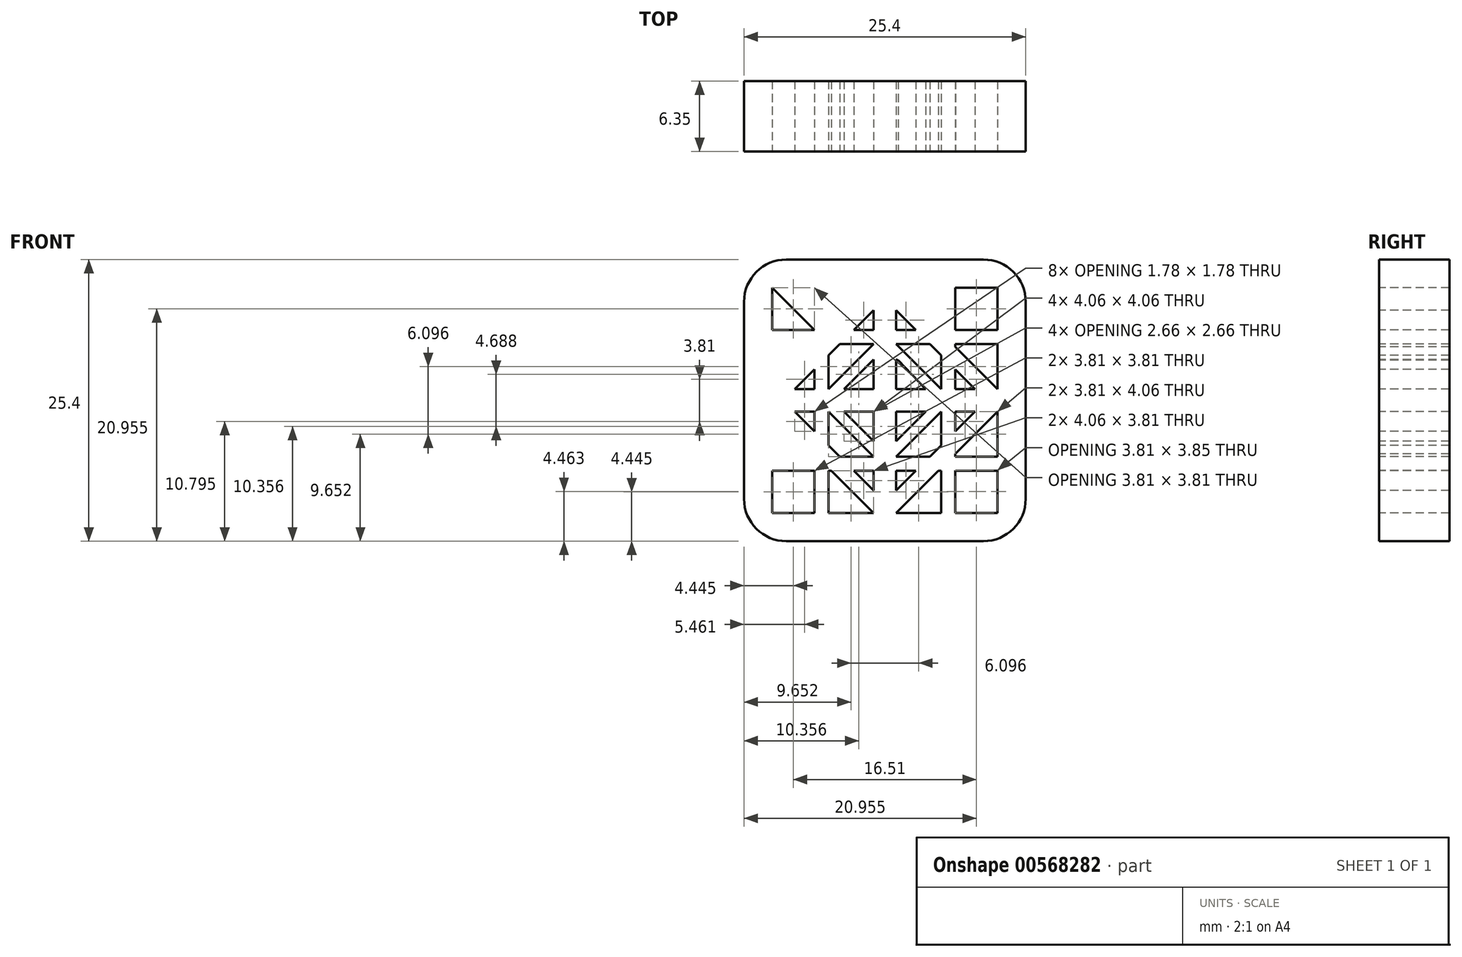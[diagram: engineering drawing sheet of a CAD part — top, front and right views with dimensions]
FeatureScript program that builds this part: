
annotation { "Feature Type Name" : "Feature", "Feature Type Description" : "" }
export const myFeature = defineFeature(function(context is Context, id is Id, definition is map)
    precondition{}
    {
        {
            var Q0;
            Q0=qCreatedBy(makeId("Front.planeOp"),FACE);
            var sketch = newSketch(context, id + "F0", { "sketchPlane" : qUnion([Q0])});
            skLineSegment(sketch, "E0", {"start": v(0, 0) * mm, "end": v(0, 25.4) * mm});
            skLineSegment(sketch, "E1", {"start": v(0, 25.4) * mm, "end": v(25.4, 25.4) * mm});
            skLineSegment(sketch, "E2", {"start": v(25.4, 25.4) * mm, "end": v(25.4, 0) * mm});
            skLineSegment(sketch, "E3", {"start": v(25.4, 0) * mm, "end": v(0, 0) * mm});
            skSolve(sketch);
        }
        {
            var Q0;
            Q0 = qSketchRegion(id + "F0", true);
            extrude(context, id + "F1", {"entities" : qUnion([Q0]), "depth" : 6.35 * mm, "offsetDistance" : 25.4 * mm});
        }
        {
            var Q0;
            Q0=qCreatedBy(makeId("Front.planeOp"),FACE);
            cPlane(context, id + "F2", {"entities" : qUnion([Q0]), "cplaneType" : CPlaneType.OFFSET, "offset" : 6.35 * mm, "width" : 152.4 * mm, "height" : 152.4 * mm});
        }
        {
            var Q0;
            Q0=qCreatedBy(id+"F2.planeOp",FACE);
            var sketch = newSketch(context, id + "F3", { "sketchPlane" : qUnion([Q0])});
            skLineSegment(sketch, "E4", {"start": v(0, 3.8) * mm, "end": v(0, 21.59) * mm});
            skLineSegment(sketch, "E5", {"start": v(3.8, 25.4) * mm, "end": v(21.59, 25.4) * mm});
            skLineSegment(sketch, "E6", {"start": v(25.4, 21.59) * mm, "end": v(25.4, 3.8) * mm});
            skLineSegment(sketch, "E7", {"start": v(21.59, 0) * mm, "end": v(3.8, 0) * mm});
            skPoint(sketch, "E8.0.internal.orphan", {"position": v(0, 12.7) * mm});
            skPoint(sketch, "E8.1.internal.orphan", {"position": v(12.7, 25.4) * mm});
            skPoint(sketch, "E8.2.internal.orphan", {"position": v(25.4, 12.7) * mm});
            skPoint(sketch, "E8.3.internal.orphan", {"position": v(12.7, 0) * mm});
            skPoint(sketch, "E9.center.orphan", {"position": v(12.7, 12.7) * mm});
            skArc(sketch, "E10", {"start": v(13.9, 16.32) * mm, "mid": v(13.8, 16.35) * mm, "end": v(13.72, 16.37) * mm});
            skLineSegment(sketch, "E11", {"start": v(12.7, 19.69) * mm, "end": v(12.7, 19.05) * mm});
            skPoint(sketch, "E11.endSnap0", {"position": v(12.7, 19.69) * mm});
            skLineSegment(sketch, "E12", {"start": v(2.54, 12.7) * mm, "end": v(8.9, 12.7) * mm});
            skLineSegment(sketch, "E13", {"start": v(16.51, 12.7) * mm, "end": v(22.86, 12.7) * mm});
            skLineSegment(sketch, "E14", {"start": v(12.7, 22.86) * mm, "end": v(22.86, 12.7) * mm});
            skLineSegment(sketch, "E15", {"start": v(22.35, 12.2) * mm, "end": v(22.86, 12.7) * mm});
            skLineSegment(sketch, "E16", {"start": v(12.7, 22.86) * mm, "end": v(12.2, 22.35) * mm});
            skLineSegment(sketch, "E17", {"start": v(17.78, 17.78) * mm, "end": v(8.13, 8.13) * mm});
            skLineSegment(sketch, "E18", {"start": v(8.13, 17.27) * mm, "end": v(17.78, 7.62) * mm});
            skLineSegment(sketch, "E19", {"start": v(2.54, 12.7) * mm, "end": v(0, 12.7) * mm});
            skLineSegment(sketch, "E20", {"start": v(12.7, 22.86) * mm, "end": v(0, 22.86) * mm});
            skLineSegment(sketch, "E21", {"start": v(12.7, 22.86) * mm, "end": v(25.4, 22.86) * mm});
            skLineSegment(sketch, "E22", {"start": v(22.86, 12.7) * mm, "end": v(22.86, 25.4) * mm});
            skLineSegment(sketch, "E23", {"start": v(22.86, 12.7) * mm, "end": v(22.86, 0) * mm});
            skLineSegment(sketch, "E24", {"start": v(12.7, 2.54) * mm, "end": v(25.4, 2.54) * mm});
            skLineSegment(sketch, "E25", {"start": v(12.7, 2.54) * mm, "end": v(0, 2.54) * mm});
            skLineSegment(sketch, "E26", {"start": v(2.54, 12.7) * mm, "end": v(2.54, 0) * mm});
            skLineSegment(sketch, "E27", {"start": v(2.54, 12.7) * mm, "end": v(2.54, 25.4) * mm});
            skLineSegment(sketch, "E28", {"start": v(2.54, 22.86) * mm, "end": v(7.11, 18.29) * mm});
            skLineSegment(sketch, "E29", {"start": v(17.78, 17.78) * mm, "end": v(22.86, 22.86) * mm});
            skLineSegment(sketch, "E30", {"start": v(18.03, 7.42) * mm, "end": v(22.86, 2.54) * mm});
            skLineSegment(sketch, "E31", {"start": v(2.54, 2.54) * mm, "end": v(7.11, 7.11) * mm});
            skLineSegment(sketch, "E32", {"start": v(22.86, 12.7) * mm, "end": v(25.4, 12.7) * mm});
            skLineSegment(sketch, "E33", {"start": v(2.54, 22.86) * mm, "end": v(12.7, 22.86) * mm});
            skLineSegment(sketch, "E34", {"start": v(12.7, 22.86) * mm, "end": v(22.86, 22.86) * mm});
            skLineSegment(sketch, "E35", {"start": v(22.86, 22.86) * mm, "end": v(22.86, 12.7) * mm});
            skLineSegment(sketch, "E36", {"start": v(22.86, 12.7) * mm, "end": v(22.86, 2.54) * mm});
            skLineSegment(sketch, "E37", {"start": v(6.35, 22.86) * mm, "end": v(6.35, 17.53) * mm});
            skLineSegment(sketch, "E38", {"start": v(6.35, 2.54) * mm, "end": v(7.62, 2.54) * mm});
            skLineSegment(sketch, "E39", {"start": v(7.62, 2.54) * mm, "end": v(7.62, 6.6) * mm});
            skLineSegment(sketch, "E40", {"start": v(7.62, 22.86) * mm, "end": v(6.35, 22.86) * mm});
            skLineSegment(sketch, "E41", {"start": v(19.05, 22.86) * mm, "end": v(19.05, 2.54) * mm});
            skLineSegment(sketch, "E42", {"start": v(19.05, 2.54) * mm, "end": v(17.78, 2.54) * mm});
            skLineSegment(sketch, "E43", {"start": v(17.78, 2.54) * mm, "end": v(17.78, 22.86) * mm});
            skLineSegment(sketch, "E44", {"start": v(17.78, 22.86) * mm, "end": v(19.05, 22.86) * mm});
            skLineSegment(sketch, "E45", {"start": v(2.54, 19.05) * mm, "end": v(7.87, 19.05) * mm});
            skLineSegment(sketch, "E46", {"start": v(22.86, 19.05) * mm, "end": v(22.86, 17.78) * mm});
            skLineSegment(sketch, "E47", {"start": v(22.86, 17.78) * mm, "end": v(8.64, 17.78) * mm});
            skLineSegment(sketch, "E48", {"start": v(2.54, 17.78) * mm, "end": v(2.54, 19.05) * mm});
            skLineSegment(sketch, "E49", {"start": v(2.54, 6.35) * mm, "end": v(22.86, 6.35) * mm});
            skLineSegment(sketch, "E50", {"start": v(22.86, 6.35) * mm, "end": v(22.86, 7.62) * mm});
            skLineSegment(sketch, "E51", {"start": v(22.86, 7.62) * mm, "end": v(8.64, 7.62) * mm});
            skLineSegment(sketch, "E52", {"start": v(2.54, 7.62) * mm, "end": v(2.54, 6.35) * mm});
            skLineSegment(sketch, "E53", {"start": v(7.62, 22.86) * mm, "end": v(12.7, 22.86) * mm});
            skLineSegment(sketch, "E54", {"start": v(17.78, 22.86) * mm, "end": v(17.78, 17.78) * mm});
            skLineSegment(sketch, "E55", {"start": v(17.78, 12.7) * mm, "end": v(17.78, 7.62) * mm});
            skLineSegment(sketch, "E56", {"start": v(11.68, 20.83) * mm, "end": v(11.68, 4.57) * mm});
            skLineSegment(sketch, "E57", {"start": v(11.68, 2.54) * mm, "end": v(13.72, 2.54) * mm});
            skLineSegment(sketch, "E58", {"start": v(13.72, 2.54) * mm, "end": v(13.72, 22.86) * mm});
            skLineSegment(sketch, "E59", {"start": v(13.72, 22.86) * mm, "end": v(11.68, 22.86) * mm});
            skLineSegment(sketch, "E60.trimOffspring", {"start": v(12.7, 17.78) * mm, "end": v(12.7, 16.51) * mm});
            skLineSegment(sketch, "E61.trimOffspring", {"start": v(12.7, 19.05) * mm, "end": v(12.7, 19.69) * mm});
            skLineSegment(sketch, "E62", {"start": v(2.54, 17.78) * mm, "end": v(2.54, 12.7) * mm});
            skLineSegment(sketch, "E63", {"start": v(2.54, 7.62) * mm, "end": v(2.54, 12.7) * mm});
            skLineSegment(sketch, "E64", {"start": v(4.57, 11.68) * mm, "end": v(20.83, 11.68) * mm});
            skLineSegment(sketch, "E65", {"start": v(22.86, 11.68) * mm, "end": v(22.86, 13.72) * mm});
            skLineSegment(sketch, "E66", {"start": v(22.86, 13.72) * mm, "end": v(4.57, 13.72) * mm});
            skLineSegment(sketch, "E67", {"start": v(2.54, 13.72) * mm, "end": v(2.54, 11.68) * mm});
            skPoint(sketch, "E68.visualSharp", {"position": v(0, 25.4) * mm});
            skArc(sketch, "E68.filletArc", {"start": v(3.81, 25.4) * mm, "mid": v(1.12, 24.28) * mm, "end": v(0, 21.59) * mm});
            skPoint(sketch, "E69.visualSharp", {"position": v(25.4, 25.4) * mm});
            skArc(sketch, "E69.filletArc", {"start": v(25.4, 21.59) * mm, "mid": v(24.28, 24.28) * mm, "end": v(21.59, 25.4) * mm});
            skPoint(sketch, "E70.visualSharp", {"position": v(25.4, 0) * mm});
            skArc(sketch, "E70.filletArc", {"start": v(21.59, 0) * mm, "mid": v(24.28, 1.12) * mm, "end": v(25.4, 3.8) * mm});
            skPoint(sketch, "E71.visualSharp", {"position": v(0, 0) * mm});
            skArc(sketch, "E71.filletArc", {"start": v(0, 3.8) * mm, "mid": v(1.12, 1.12) * mm, "end": v(3.8, 0) * mm});
            skLineSegment(sketch, "E72", {"start": v(12.7, 21.84) * mm, "end": v(21.84, 12.7) * mm});
            skLineSegment(sketch, "E73", {"start": v(22.86, 13.72) * mm, "end": v(13.72, 22.86) * mm});
            skLineSegment(sketch, "E74", {"start": v(11.68, 22.86) * mm, "end": v(13.72, 22.86) * mm});
            skLineSegment(sketch, "E75", {"start": v(12.7, 3.56) * mm, "end": v(22.86, 13.72) * mm});
            skLineSegment(sketch, "E76", {"start": v(22.86, 11.68) * mm, "end": v(13.72, 2.54) * mm});
            skLineSegment(sketch, "E77", {"start": v(2.54, 11.68) * mm, "end": v(11.68, 2.54) * mm});
            skLineSegment(sketch, "E78", {"start": v(3.56, 12.7) * mm, "end": v(12.7, 3.56) * mm});
            skLineSegment(sketch, "E79", {"start": v(2.54, 11.68) * mm, "end": v(2.54, 13.72) * mm});
            skLineSegment(sketch, "E80", {"start": v(2.54, 13.72) * mm, "end": v(11.68, 22.86) * mm});
            skLineSegment(sketch, "E81", {"start": v(13.72, 22.86) * mm, "end": v(13.2, 22.35) * mm});
            skLineSegment(sketch, "E82.trimOffspring", {"start": v(6.6, 7.62) * mm, "end": v(2.54, 7.62) * mm});
            skLineSegment(sketch, "E83.bottom", {"start": v(0, 0) * mm, "end": v(25.4, 0) * mm});
            skLineSegment(sketch, "E83.top", {"start": v(0, 25.4) * mm, "end": v(25.4, 25.4) * mm});
            skLineSegment(sketch, "E83.left", {"start": v(0, 0) * mm, "end": v(0, 25.4) * mm});
            skLineSegment(sketch, "E83.right", {"start": v(25.4, 0) * mm, "end": v(25.4, 25.4) * mm});
            skLineSegment(sketch, "E84.trimOffspring", {"start": v(22.35, 12.2) * mm, "end": v(22.86, 11.68) * mm});
            skLineSegment(sketch, "E85.trimOffspring", {"start": v(7.62, 8.64) * mm, "end": v(7.62, 16.76) * mm});
            skPoint(sketch, "E86.orphan", {"position": v(7.62, 7.62) * mm});
            skLineSegment(sketch, "E87.trimOffspring", {"start": v(6.35, 15.5) * mm, "end": v(6.35, 2.54) * mm});
            skLineSegment(sketch, "E88.trimOffspring", {"start": v(6.6, 17.78) * mm, "end": v(2.54, 17.78) * mm});
            skLineSegment(sketch, "E89.trimOffspring", {"start": v(7.62, 18.8) * mm, "end": v(7.62, 22.86) * mm});
            skPoint(sketch, "E90.orphan", {"position": v(7.62, 17.78) * mm});
            skLineSegment(sketch, "E91.trimOffspring", {"start": v(9.9, 19.05) * mm, "end": v(22.86, 19.05) * mm});
            skLineSegment(sketch, "E92.trimOffspring", {"start": v(12.7, 21.84) * mm, "end": v(3.56, 12.7) * mm});
            skLineSegment(sketch, "E93.trimOffspring", {"start": v(15.08, 15.08) * mm, "end": v(16.37, 13.72) * mm});
            skPoint(sketch, "E94.start.orphan", {"position": v(13.72, 16.51) * mm});
            skLineSegment(sketch, "E95", {"start": v(13.72, 16.51) * mm, "end": v(16.37, 13.72) * mm});
            skLineSegment(sketch, "E96", {"start": v(13.72, 17.78) * mm, "end": v(17.78, 13.72) * mm});
            skLineSegment(sketch, "E97", {"start": v(17.78, 13.72) * mm, "end": v(16.37, 13.72) * mm});
            skLineSegment(sketch, "E98", {"start": v(13.72, 16.51) * mm, "end": v(13.72, 17.78) * mm});
            skLineSegment(sketch, "E99", {"start": v(13.72, 9.03) * mm, "end": v(16.37, 11.68) * mm});
            skLineSegment(sketch, "E100", {"start": v(13.72, 7.62) * mm, "end": v(13.72, 9.03) * mm});
            skLineSegment(sketch, "E101", {"start": v(17.78, 11.68) * mm, "end": v(13.72, 7.62) * mm});
            skLineSegment(sketch, "E102", {"start": v(16.37, 11.68) * mm, "end": v(17.78, 11.68) * mm});
            skLineSegment(sketch, "E103", {"start": v(7.62, 12.7) * mm, "end": v(8.9, 12.7) * mm});
            skLineSegment(sketch, "E104", {"start": v(11.68, 16.37) * mm, "end": v(11.68, 17.78) * mm});
            skLineSegment(sketch, "E105", {"start": v(7.62, 11.68) * mm, "end": v(11.68, 7.62) * mm});
            skLineSegment(sketch, "E106", {"start": v(11.68, 7.62) * mm, "end": v(11.68, 9.03) * mm});
            skLineSegment(sketch, "E107", {"start": v(9.03, 11.68) * mm, "end": v(11.68, 9.03) * mm});
            skLineSegment(sketch, "E108", {"start": v(9.03, 11.68) * mm, "end": v(7.62, 11.68) * mm});
            skArc(sketch, "E109.trimOffspring", {"start": v(9.03, 13.72) * mm, "mid": v(11.68, 9.03) * mm, "end": v(16.37, 11.68) * mm});
            skLineSegment(sketch, "E110", {"start": v(9.03, 13.72) * mm, "end": v(11.68, 16.37) * mm});
            skLineSegment(sketch, "E111", {"start": v(11.68, 17.78) * mm, "end": v(11.68, 16.37) * mm});
            skLineSegment(sketch, "E112", {"start": v(7.62, 13.72) * mm, "end": v(11.68, 17.78) * mm});
            skLineSegment(sketch, "E113", {"start": v(7.62, 13.72) * mm, "end": v(9.03, 13.72) * mm});
            skSolve(sketch);
        }
        {
            var Q0;
            {var subQ0=sQuery(id+"F3.wireOp",EDGE,"E33");Q0=makeQuery(id+"F3.imprint","IMPRINT",FACE,{"disambiguationData":[TD([[makeQuery(id+"F3.imprint","IMPRINT",EDGE,{"derivedFrom":subQ0}),-1.0]])]});}
            var Q1;
            {var subQ1=sQuery(id+"F3.wireOp",EDGE,"E27");var subQ3=sQuery(id+"F3.wireOp",EDGE,"E45");var subQ4=makeQuery(id+"F3.imprint","INTERSECT",VERTEX,{"derivedFrom":[subQ1,subQ3,sQuery(id+"F3.wireOp",EDGE,"E48")]});Q1=makeQuery(id+"F3.imprint","IMPRINT",FACE,{"disambiguationData":[TD([[makeQuery(id+"F3.imprint","IMPRINT",EDGE,{"disambiguationData":[TD([[subQ4,-1.0]])],"derivedFrom":subQ3}),1.0]])]});}
            var Q2;
            {var subQ5=sQuery(id+"F3.wireOp",EDGE,"E62");Q2=makeQuery(id+"F3.imprint","IMPRINT",FACE,{"disambiguationData":[TD([[makeQuery(id+"F3.imprint","IMPRINT",EDGE,{"derivedFrom":subQ5}),1.0]])]});}
            var Q3;
            {var subQ0=sQuery(id+"F3.wireOp",EDGE,"E92.trimOffspring");var subQ1=sQuery(id+"F3.wireOp",EDGE,"E66");var subQ2=makeQuery(id+"F3.imprint","INTERSECT",VERTEX,{"derivedFrom":[subQ1,subQ0]});Q3=makeQuery(id+"F3.imprint","IMPRINT",FACE,{"disambiguationData":[TD([[makeQuery(id+"F3.imprint","IMPRINT",EDGE,{"disambiguationData":[TD([[subQ2,1.0]])],"derivedFrom":subQ1}),-1.0]])]});}
            var Q4;
            {var subQ0=sQuery(id+"F3.wireOp",EDGE,"E78");var subQ1=sQuery(id+"F3.wireOp",EDGE,"E64");var subQ2=makeQuery(id+"F3.imprint","INTERSECT",VERTEX,{"derivedFrom":[subQ1,subQ0]});Q4=makeQuery(id+"F3.imprint","IMPRINT",FACE,{"disambiguationData":[TD([[makeQuery(id+"F3.imprint","IMPRINT",EDGE,{"disambiguationData":[TD([[subQ2,-1.0]])],"derivedFrom":subQ1}),-1.0]])]});}
            var Q5;
            {var subQ0=sQuery(id+"F3.wireOp",EDGE,"E63");Q5=makeQuery(id+"F3.imprint","IMPRINT",FACE,{"disambiguationData":[TD([[makeQuery(id+"F3.imprint","IMPRINT",EDGE,{"derivedFrom":subQ0}),-1.0]])]});}
            var Q6;
            {var subQ0=sQuery(id+"F3.wireOp",EDGE,"E107");var subQ1=sQuery(id+"F3.wireOp",EDGE,"E17");var subQ2=makeQuery(id+"F3.imprint","INTERSECT",VERTEX,{"derivedFrom":[subQ1,subQ0]});Q6=makeQuery(id+"F3.imprint","IMPRINT",FACE,{"disambiguationData":[TD([[makeQuery(id+"F3.imprint","IMPRINT",EDGE,{"disambiguationData":[TD([[subQ2,1.0]])],"derivedFrom":subQ1}),-1.0]])]});}
            var Q7;
            {var subQ0=sQuery(id+"F3.wireOp",EDGE,"E107");var subQ1=sQuery(id+"F3.wireOp",EDGE,"E17");var subQ2=makeQuery(id+"F3.imprint","INTERSECT",VERTEX,{"derivedFrom":[subQ1,subQ0]});Q7=makeQuery(id+"F3.imprint","IMPRINT",FACE,{"disambiguationData":[TD([[makeQuery(id+"F3.imprint","IMPRINT",EDGE,{"disambiguationData":[TD([[subQ2,1.0]])],"derivedFrom":subQ1}),1.0]])]});}
            var Q8;
            {var subQ0=sQuery(id+"F3.wireOp",EDGE,"E10");Q8=makeQuery(id+"F3.imprint","IMPRINT",FACE,{"disambiguationData":[TD([[makeQuery(id+"F3.imprint","IMPRINT",EDGE,{"derivedFrom":subQ0}),1.0]])]});}
            var Q9;
            {var subQ0=sQuery(id+"F3.wireOp",EDGE,"E95");var subQ1=sQuery(id+"F3.wireOp",EDGE,"E17");var subQ2=makeQuery(id+"F3.imprint","INTERSECT",VERTEX,{"derivedFrom":[subQ1,subQ0]});Q9=makeQuery(id+"F3.imprint","IMPRINT",FACE,{"disambiguationData":[TD([[makeQuery(id+"F3.imprint","IMPRINT",EDGE,{"disambiguationData":[TD([[subQ2,-1.0]])],"derivedFrom":subQ1}),1.0]])]});}
            var Q10;
            {var subQ0=sQuery(id+"F3.wireOp",EDGE,"E99");var subQ1=sQuery(id+"F3.wireOp",EDGE,"E18");var subQ2=makeQuery(id+"F3.imprint","INTERSECT",VERTEX,{"derivedFrom":[subQ1,subQ0]});Q10=makeQuery(id+"F3.imprint","IMPRINT",FACE,{"disambiguationData":[TD([[makeQuery(id+"F3.imprint","IMPRINT",EDGE,{"disambiguationData":[TD([[subQ2,1.0]])],"derivedFrom":subQ1}),1.0]])]});}
            var Q11;
            {var subQ0=sQuery(id+"F3.wireOp",EDGE,"E99");var subQ1=sQuery(id+"F3.wireOp",EDGE,"E18");var subQ2=makeQuery(id+"F3.imprint","INTERSECT",VERTEX,{"derivedFrom":[subQ1,subQ0]});Q11=makeQuery(id+"F3.imprint","IMPRINT",FACE,{"disambiguationData":[TD([[makeQuery(id+"F3.imprint","IMPRINT",EDGE,{"disambiguationData":[TD([[subQ2,1.0]])],"derivedFrom":subQ1}),-1.0]])]});}
            var Q12;
            {var subQ0=sQuery(id+"F3.wireOp",EDGE,"E78");var subQ1=sQuery(id+"F3.wireOp",EDGE,"E17");var subQ2=makeQuery(id+"F3.imprint","INTERSECT",VERTEX,{"derivedFrom":[subQ1,subQ0]});Q12=makeQuery(id+"F3.imprint","IMPRINT",FACE,{"disambiguationData":[TD([[makeQuery(id+"F3.imprint","IMPRINT",EDGE,{"disambiguationData":[TD([[subQ2,1.0]])],"derivedFrom":subQ1}),1.0]])]});}
            var Q13;
            {var subQ0=sQuery(id+"F3.wireOp",EDGE,"E78");var subQ1=sQuery(id+"F3.wireOp",EDGE,"E17");var subQ2=makeQuery(id+"F3.imprint","INTERSECT",VERTEX,{"derivedFrom":[subQ1,subQ0]});Q13=makeQuery(id+"F3.imprint","IMPRINT",FACE,{"disambiguationData":[TD([[makeQuery(id+"F3.imprint","IMPRINT",EDGE,{"disambiguationData":[TD([[subQ2,1.0]])],"derivedFrom":subQ1}),-1.0]])]});}
            var Q14;
            {var subQ0=sQuery(id+"F3.wireOp",EDGE,"E72");var subQ1=sQuery(id+"F3.wireOp",EDGE,"E17");var subQ2=makeQuery(id+"F3.imprint","INTERSECT",VERTEX,{"derivedFrom":[subQ1,subQ0]});Q14=makeQuery(id+"F3.imprint","IMPRINT",FACE,{"disambiguationData":[TD([[makeQuery(id+"F3.imprint","IMPRINT",EDGE,{"disambiguationData":[TD([[subQ2,-1.0]])],"derivedFrom":subQ1}),-1.0]])]});}
            var Q15;
            {var subQ0=sQuery(id+"F3.wireOp",EDGE,"E72");var subQ1=sQuery(id+"F3.wireOp",EDGE,"E17");var subQ2=makeQuery(id+"F3.imprint","INTERSECT",VERTEX,{"derivedFrom":[subQ1,subQ0]});Q15=makeQuery(id+"F3.imprint","IMPRINT",FACE,{"disambiguationData":[TD([[makeQuery(id+"F3.imprint","IMPRINT",EDGE,{"disambiguationData":[TD([[subQ2,-1.0]])],"derivedFrom":subQ1}),1.0]])]});}
            var Q16;
            {var subQ0=sQuery(id+"F3.wireOp",EDGE,"E101");var subQ1=sQuery(id+"F3.wireOp",EDGE,"E18");var subQ2=makeQuery(id+"F3.imprint","INTERSECT",VERTEX,{"derivedFrom":[subQ1,subQ0]});Q16=makeQuery(id+"F3.imprint","IMPRINT",FACE,{"disambiguationData":[TD([[makeQuery(id+"F3.imprint","IMPRINT",EDGE,{"disambiguationData":[TD([[subQ2,-1.0]])],"derivedFrom":subQ1}),1.0]])]});}
            var Q17;
            {var subQ0=sQuery(id+"F3.wireOp",EDGE,"E101");var subQ1=sQuery(id+"F3.wireOp",EDGE,"E18");var subQ2=makeQuery(id+"F3.imprint","INTERSECT",VERTEX,{"derivedFrom":[subQ1,subQ0]});Q17=makeQuery(id+"F3.imprint","IMPRINT",FACE,{"disambiguationData":[TD([[makeQuery(id+"F3.imprint","IMPRINT",EDGE,{"disambiguationData":[TD([[subQ2,-1.0]])],"derivedFrom":subQ1}),-1.0]])]});}
            var Q18;
            {var subQ0=sQuery(id+"F3.wireOp",EDGE,"E58");var subQ1=sQuery(id+"F3.wireOp",EDGE,"E49");var subQ2=makeQuery(id+"F3.imprint","INTERSECT",VERTEX,{"derivedFrom":[subQ1,subQ0]});Q18=makeQuery(id+"F3.imprint","IMPRINT",FACE,{"disambiguationData":[TD([[makeQuery(id+"F3.imprint","IMPRINT",EDGE,{"disambiguationData":[TD([[subQ2,-1.0]])],"derivedFrom":subQ1}),-1.0]])]});}
            var Q19;
            {var subQ0=sQuery(id+"F3.wireOp",EDGE,"E78");var subQ1=sQuery(id+"F3.wireOp",EDGE,"E49");var subQ2=makeQuery(id+"F3.imprint","INTERSECT",VERTEX,{"derivedFrom":[subQ1,subQ0]});Q19=makeQuery(id+"F3.imprint","IMPRINT",FACE,{"disambiguationData":[TD([[makeQuery(id+"F3.imprint","IMPRINT",EDGE,{"disambiguationData":[TD([[subQ2,-1.0]])],"derivedFrom":subQ1}),-1.0]])]});}
            var Q20;
            {var subQ3=sQuery(id+"F3.wireOp",EDGE,"E39");var subQ5=sQuery(id+"F3.wireOp",EDGE,"E49");var subQ6=makeQuery(id+"F3.imprint","INTERSECT",VERTEX,{"derivedFrom":[subQ3,subQ5]});Q20=makeQuery(id+"F3.imprint","IMPRINT",FACE,{"disambiguationData":[TD([[makeQuery(id+"F3.imprint","IMPRINT",EDGE,{"disambiguationData":[TD([[subQ6,-1.0]])],"derivedFrom":subQ5}),-1.0]])]});}
            var Q21;
            {var subQ0=sQuery(id+"F3.wireOp",EDGE,"E31");var subQ1=sQuery(id+"F3.wireOp",EDGE,"E25");var subQ2=makeQuery(id+"F3.imprint","INTERSECT",VERTEX,{"derivedFrom":[subQ1,sQuery(id+"F3.wireOp",EDGE,"E26"),subQ0]});Q21=makeQuery(id+"F3.imprint","IMPRINT",FACE,{"disambiguationData":[TD([[makeQuery(id+"F3.imprint","IMPRINT",EDGE,{"disambiguationData":[TD([[subQ2,1.0]])],"derivedFrom":subQ1}),-1.0]])]});}
            var Q22;
            {var subQ0=sQuery(id+"F3.wireOp",EDGE,"E49");var subQ1=sQuery(id+"F3.wireOp",EDGE,"E26");var subQ2=makeQuery(id+"F3.imprint","INTERSECT",VERTEX,{"derivedFrom":[subQ1,subQ0,sQuery(id+"F3.wireOp",EDGE,"E52")]});Q22=makeQuery(id+"F3.imprint","IMPRINT",FACE,{"disambiguationData":[TD([[makeQuery(id+"F3.imprint","IMPRINT",EDGE,{"disambiguationData":[TD([[subQ2,-1.0]])],"derivedFrom":subQ1}),1.0]])]});}
            var Q23;
            {var subQ3=sQuery(id+"F3.wireOp",EDGE,"E43");var subQ5=sQuery(id+"F3.wireOp",EDGE,"E49");var subQ6=makeQuery(id+"F3.imprint","INTERSECT",VERTEX,{"derivedFrom":[subQ3,subQ5]});Q23=makeQuery(id+"F3.imprint","IMPRINT",FACE,{"disambiguationData":[TD([[makeQuery(id+"F3.imprint","IMPRINT",EDGE,{"disambiguationData":[TD([[subQ6,1.0]])],"derivedFrom":subQ5}),-1.0]])]});}
            var Q24;
            {var subQ0=sQuery(id+"F3.wireOp",EDGE,"E30");var subQ5=sQuery(id+"F3.wireOp",EDGE,"E49");var subQ6=makeQuery(id+"F3.imprint","INTERSECT",VERTEX,{"derivedFrom":[subQ0,subQ5]});Q24=makeQuery(id+"F3.imprint","IMPRINT",FACE,{"disambiguationData":[TD([[makeQuery(id+"F3.imprint","IMPRINT",EDGE,{"disambiguationData":[TD([[subQ6,1.0]])],"derivedFrom":subQ5}),-1.0]])]});}
            var Q25;
            {var subQ1=sQuery(id+"F3.wireOp",EDGE,"E30");var subQ3=sQuery(id+"F3.wireOp",EDGE,"E49");var subQ4=makeQuery(id+"F3.imprint","INTERSECT",VERTEX,{"derivedFrom":[subQ1,subQ3]});Q25=makeQuery(id+"F3.imprint","IMPRINT",FACE,{"disambiguationData":[TD([[makeQuery(id+"F3.imprint","IMPRINT",EDGE,{"disambiguationData":[TD([[subQ4,-1.0]])],"derivedFrom":subQ3}),-1.0]])]});}
            var Q26;
            {var subQ0=sQuery(id+"F3.wireOp",EDGE,"E76");var subQ5=sQuery(id+"F3.wireOp",EDGE,"E41");var subQ6=makeQuery(id+"F3.imprint","INTERSECT",VERTEX,{"derivedFrom":[subQ5,subQ0]});Q26=makeQuery(id+"F3.imprint","IMPRINT",FACE,{"disambiguationData":[TD([[makeQuery(id+"F3.imprint","IMPRINT",EDGE,{"disambiguationData":[TD([[subQ6,-1.0]])],"derivedFrom":subQ5}),1.0]])]});}
            var Q27;
            {var subQ0=sQuery(id+"F3.wireOp",EDGE,"E64");var subQ1=sQuery(id+"F3.wireOp",EDGE,"E41");var subQ2=makeQuery(id+"F3.imprint","INTERSECT",VERTEX,{"derivedFrom":[subQ1,subQ0]});Q27=makeQuery(id+"F3.imprint","IMPRINT",FACE,{"disambiguationData":[TD([[makeQuery(id+"F3.imprint","IMPRINT",EDGE,{"disambiguationData":[TD([[subQ2,-1.0]])],"derivedFrom":subQ1}),1.0]])]});}
            var Q28;
            {var subQ0=sQuery(id+"F3.wireOp",EDGE,"E72");var subQ1=sQuery(id+"F3.wireOp",EDGE,"E41");var subQ2=makeQuery(id+"F3.imprint","INTERSECT",VERTEX,{"derivedFrom":[subQ1,subQ0]});Q28=makeQuery(id+"F3.imprint","IMPRINT",FACE,{"disambiguationData":[TD([[makeQuery(id+"F3.imprint","IMPRINT",EDGE,{"disambiguationData":[TD([[subQ2,-1.0]])],"derivedFrom":subQ1}),1.0]])]});}
            var Q29;
            {var subQ3=sQuery(id+"F3.wireOp",EDGE,"E47");var subQ5=sQuery(id+"F3.wireOp",EDGE,"E41");var subQ6=makeQuery(id+"F3.imprint","INTERSECT",VERTEX,{"derivedFrom":[subQ5,subQ3]});Q29=makeQuery(id+"F3.imprint","IMPRINT",FACE,{"disambiguationData":[TD([[makeQuery(id+"F3.imprint","IMPRINT",EDGE,{"disambiguationData":[TD([[subQ6,-1.0]])],"derivedFrom":subQ5}),1.0]])]});}
            var Q30;
            {var subQ0=sQuery(id+"F3.wireOp",EDGE,"E35");var subQ3=sQuery(id+"F3.wireOp",EDGE,"E91.trimOffspring");var subQ5=makeQuery(id+"F3.imprint","INTERSECT",VERTEX,{"derivedFrom":[subQ0,sQuery(id+"F3.wireOp",EDGE,"E46"),subQ3]});Q30=makeQuery(id+"F3.imprint","IMPRINT",FACE,{"disambiguationData":[TD([[makeQuery(id+"F3.imprint","IMPRINT",EDGE,{"disambiguationData":[TD([[subQ5,1.0]])],"derivedFrom":subQ3}),1.0]])]});}
            var Q31;
            {var subQ0=sQuery(id+"F3.wireOp",EDGE,"E34");var subQ3=sQuery(id+"F3.wireOp",EDGE,"E41");var subQ5=makeQuery(id+"F3.imprint","INTERSECT",VERTEX,{"derivedFrom":[subQ0,subQ3,sQuery(id+"F3.wireOp",EDGE,"E44")]});Q31=makeQuery(id+"F3.imprint","IMPRINT",FACE,{"disambiguationData":[TD([[makeQuery(id+"F3.imprint","IMPRINT",EDGE,{"disambiguationData":[TD([[subQ5,-1.0]])],"derivedFrom":subQ3}),1.0]])]});}
            var Q32;
            {var subQ3=sQuery(id+"F3.wireOp",EDGE,"E54");var subQ5=sQuery(id+"F3.wireOp",EDGE,"E91.trimOffspring");var subQ6=makeQuery(id+"F3.imprint","INTERSECT",VERTEX,{"derivedFrom":[subQ3,subQ5]});Q32=makeQuery(id+"F3.imprint","IMPRINT",FACE,{"disambiguationData":[TD([[makeQuery(id+"F3.imprint","IMPRINT",EDGE,{"disambiguationData":[TD([[subQ6,1.0]])],"derivedFrom":subQ5}),1.0]])]});}
            var Q33;
            {var subQ0=sQuery(id+"F3.wireOp",EDGE,"E91.trimOffspring");var subQ1=sQuery(id+"F3.wireOp",EDGE,"E58");var subQ2=makeQuery(id+"F3.imprint","INTERSECT",VERTEX,{"derivedFrom":[subQ1,subQ0]});Q33=makeQuery(id+"F3.imprint","IMPRINT",FACE,{"disambiguationData":[TD([[makeQuery(id+"F3.imprint","IMPRINT",EDGE,{"disambiguationData":[TD([[subQ2,-1.0]])],"derivedFrom":subQ1}),-1.0]])]});}
            var Q34;
            {var subQ0=sQuery(id+"F3.wireOp",EDGE,"E92.trimOffspring");var subQ1=sQuery(id+"F3.wireOp",EDGE,"E56");var subQ2=makeQuery(id+"F3.imprint","INTERSECT",VERTEX,{"derivedFrom":[subQ1,subQ0]});Q34=makeQuery(id+"F3.imprint","IMPRINT",FACE,{"disambiguationData":[TD([[makeQuery(id+"F3.imprint","IMPRINT",EDGE,{"disambiguationData":[TD([[subQ2,-1.0]])],"derivedFrom":subQ1}),-1.0]])]});}
            var Q35;
            {var subQ5=sQuery(id+"F3.wireOp",EDGE,"E53");Q35=makeQuery(id+"F3.imprint","IMPRINT",FACE,{"disambiguationData":[TD([[makeQuery(id+"F3.imprint","IMPRINT",EDGE,{"derivedFrom":subQ5}),-1.0]])]});}
            var Q36;
            {var subQ0=sQuery(id+"F3.wireOp",EDGE,"E92.trimOffspring");var subQ1=sQuery(id+"F3.wireOp",EDGE,"E18");var subQ2=makeQuery(id+"F3.imprint","INTERSECT",VERTEX,{"derivedFrom":[subQ1,subQ0]});Q36=makeQuery(id+"F3.imprint","IMPRINT",FACE,{"disambiguationData":[TD([[makeQuery(id+"F3.imprint","IMPRINT",EDGE,{"disambiguationData":[TD([[subQ2,-1.0]])],"derivedFrom":subQ1}),-1.0]])]});}
            var Q37;
            {var subQ0=sQuery(id+"F3.wireOp",EDGE,"E92.trimOffspring");var subQ1=sQuery(id+"F3.wireOp",EDGE,"E18");var subQ2=makeQuery(id+"F3.imprint","INTERSECT",VERTEX,{"derivedFrom":[subQ1,subQ0]});Q37=makeQuery(id+"F3.imprint","IMPRINT",FACE,{"disambiguationData":[TD([[makeQuery(id+"F3.imprint","IMPRINT",EDGE,{"disambiguationData":[TD([[subQ2,-1.0]])],"derivedFrom":subQ1}),1.0]])]});}
            var Q38;
            {var subQ0=sQuery(id+"F3.wireOp",EDGE,"E110");var subQ1=sQuery(id+"F3.wireOp",EDGE,"E18");var subQ2=makeQuery(id+"F3.imprint","INTERSECT",VERTEX,{"derivedFrom":[subQ1,subQ0]});Q38=makeQuery(id+"F3.imprint","IMPRINT",FACE,{"disambiguationData":[TD([[makeQuery(id+"F3.imprint","IMPRINT",EDGE,{"disambiguationData":[TD([[subQ2,-1.0]])],"derivedFrom":subQ1}),1.0]])]});}
            var Q39;
            {var subQ0=sQuery(id+"F3.wireOp",EDGE,"E110");var subQ1=sQuery(id+"F3.wireOp",EDGE,"E18");var subQ2=makeQuery(id+"F3.imprint","INTERSECT",VERTEX,{"derivedFrom":[subQ1,subQ0]});Q39=makeQuery(id+"F3.imprint","IMPRINT",FACE,{"disambiguationData":[TD([[makeQuery(id+"F3.imprint","IMPRINT",EDGE,{"disambiguationData":[TD([[subQ2,-1.0]])],"derivedFrom":subQ1}),-1.0]])]});}
            extrude(context, id + "F4", {"entities" : qUnion([Q0, Q1, Q2, Q3, Q4, Q5, Q6, Q7, Q8, Q9, Q10, Q11, Q12, Q13, Q14, Q15, Q16, Q17, Q18, Q19, Q20, Q21, Q22, Q23, Q24, Q25, Q26, Q27, Q28, Q29, Q30, Q31, Q32, Q33, Q34, Q35, Q36, Q37, Q38, Q39]), "operationType" : NewBodyOperationType.REMOVE, "oppositeDirection" : true, "depth" : 25.4 * mm, "offsetDistance" : 25.4 * mm});
        }
        {
            var Q0;
            Q0=makeQuery(id+"F1.opExtrude","SWEPT_EDGE",EDGE,{"disambiguationData":[OSD([sQuery(id+"F0.wireOp",EDGE,"E0"),sQuery(id+"F0.wireOp",EDGE,"E1")])]});
            fillet(context, id + "F5", {"entities" : qUnion([Q0]), "radius" : 3.8 * mm, "tangentPropagation" : true, "allowEdgeOverflow" : false});
        }
        {
            var Q0;
            Q0=makeQuery(id+"F1.opExtrude","SWEPT_EDGE",EDGE,{"disambiguationData":[OSD([sQuery(id+"F0.wireOp",EDGE,"E1"),sQuery(id+"F0.wireOp",EDGE,"E2")])]});
            var Q1;
            Q1=makeQuery(id+"F1.opExtrude","SWEPT_EDGE",EDGE,{"disambiguationData":[OSD([sQuery(id+"F0.wireOp",EDGE,"E2"),sQuery(id+"F0.wireOp",EDGE,"E3")])]});
            var Q2;
            Q2=makeQuery(id+"F1.opExtrude","SWEPT_EDGE",EDGE,{"disambiguationData":[OSD([sQuery(id+"F0.wireOp",EDGE,"E0"),sQuery(id+"F0.wireOp",EDGE,"E3")])]});
            fillet(context, id + "F6", {"entities" : qUnion([Q0, Q1, Q2]), "radius" : 3.8 * mm, "tangentPropagation" : true, "allowEdgeOverflow" : false});
        }
    });
